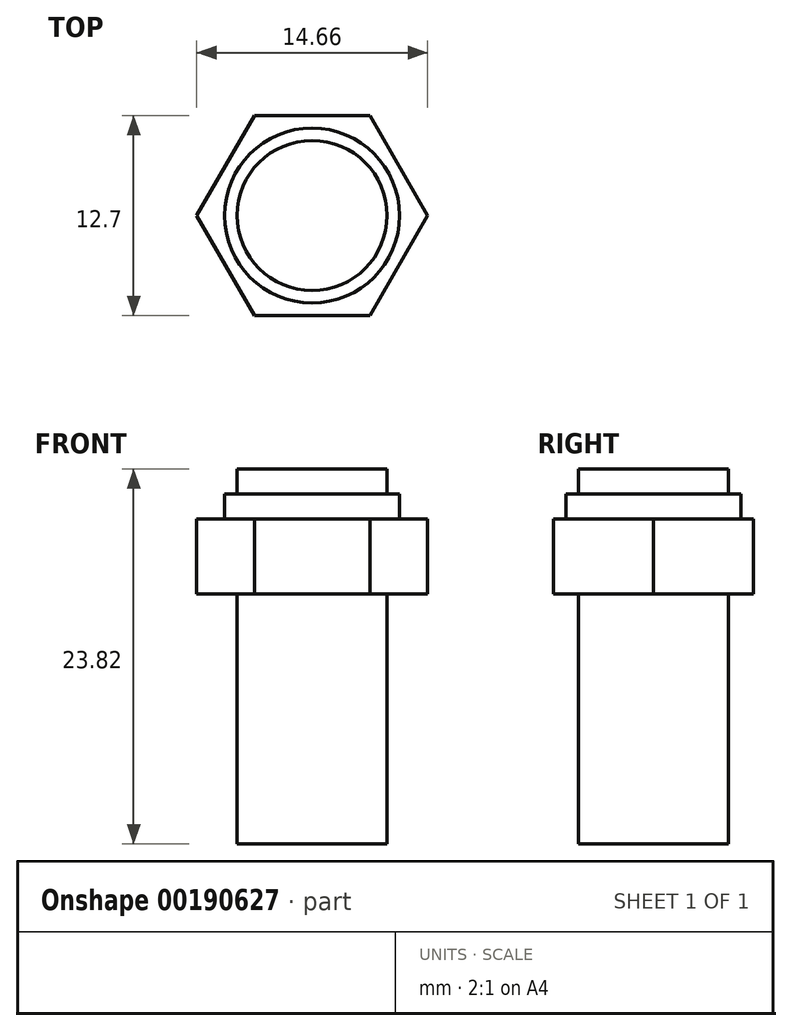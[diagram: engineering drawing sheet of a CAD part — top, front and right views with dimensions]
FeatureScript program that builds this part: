
annotation { "Feature Type Name" : "Feature", "Feature Type Description" : "" }
export const myFeature = defineFeature(function(context is Context, id is Id, definition is map)
    precondition{}
    {
        {
            var Q0;
            Q0=qCreatedBy(makeId("Top.planeOp"),FACE);
            var sketch = newSketch(context, id + "F0", { "sketchPlane" : qUnion([Q0])});
            skCircle(sketch, "E0.cCircle", {"center": v(0, 0) * mm, "radius": 6.35 * mm, "construction": true});
            skLineSegment(sketch, "E0.0", {"start": v(3.67, -6.35) * mm, "end": v(-3.67, -6.35) * mm});
            skLineSegment(sketch, "E0.1", {"start": v(-3.67, -6.35) * mm, "end": v(-7.33, 0) * mm});
            skLineSegment(sketch, "E0.2", {"start": v(-7.33, 0) * mm, "end": v(-3.67, 6.35) * mm});
            skLineSegment(sketch, "E0.3", {"start": v(-3.67, 6.35) * mm, "end": v(3.67, 6.35) * mm});
            skLineSegment(sketch, "E0.4", {"start": v(3.67, 6.35) * mm, "end": v(7.33, 0) * mm});
            skLineSegment(sketch, "E0.5", {"start": v(7.33, 0) * mm, "end": v(3.67, -6.35) * mm});
            skPoint(sketch, "E0.0.midPoint", {"position": v(0, -6.35) * mm});
            skSolve(sketch);
        }
        {
            var Q0;
            Q0 = qSketchRegion(id + "F0", true);
            extrude(context, id + "F1", {"entities" : qUnion([Q0]), "depth" : 4.76 * mm});
        }
        {
            var Q0;
            Q0=qCreatedBy(makeId("Top.planeOp"),FACE);
            var sketch = newSketch(context, id + "F2", { "sketchPlane" : qUnion([Q0])});
            skCircle(sketch, "E1", {"center": v(0, 0) * mm, "radius": 4.76 * mm});
            skSolve(sketch);
        }
        {
            var Q0;
            Q0 = qSketchRegion(id + "F2", true);
            extrude(context, id + "F3", {"entities" : qUnion([Q0]), "operationType" : NewBodyOperationType.ADD, "oppositeDirection" : true, "depth" : 15.88 * mm});
        }
        {
            var Q0;
            Q0=makeQuery(id+"F1.opExtrude","CAP_FACE",FACE,{"disambiguationData":[OSD([sQuery(id+"F0.wireOp",EDGE,"E0.0"),sQuery(id+"F0.wireOp",EDGE,"E0.1"),sQuery(id+"F0.wireOp",EDGE,"E0.2"),sQuery(id+"F0.wireOp",EDGE,"E0.3"),sQuery(id+"F0.wireOp",EDGE,"E0.4"),sQuery(id+"F0.wireOp",EDGE,"E0.5")])],"isStart":false});
            var sketch = newSketch(context, id + "F4", { "sketchPlane" : qUnion([Q0])});
            skCircle(sketch, "E2", {"center": v(0, 0) * mm, "radius": 5.56 * mm});
            skSolve(sketch);
        }
        {
            var Q0;
            Q0 = qSketchRegion(id + "F4", true);
            extrude(context, id + "F5", {"entities" : qUnion([Q0]), "operationType" : NewBodyOperationType.ADD, "depth" : 1.59 * mm});
        }
        {
            var Q0;
            Q0=makeQuery(id+"F5.opExtrude","CAP_FACE",FACE,{"disambiguationData":[OSD([sQuery(id+"F4.wireOp",EDGE,"E2")])],"isStart":false});
            var sketch = newSketch(context, id + "F6", { "sketchPlane" : qUnion([Q0])});
            skCircle(sketch, "E3", {"center": v(0, 0) * mm, "radius": 4.76 * mm});
            skSolve(sketch);
        }
        {
            var Q0;
            Q0 = qSketchRegion(id + "F6", true);
            extrude(context, id + "F7", {"entities" : qUnion([Q0]), "operationType" : NewBodyOperationType.ADD, "depth" : 1.59 * mm});
        }
    });
